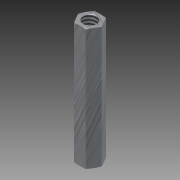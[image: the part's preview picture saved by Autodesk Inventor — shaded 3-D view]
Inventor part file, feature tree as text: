
AUTODESK INVENTOR PART (.ipt)
format: ipt  version: 2012 (Build 160160000, 160)  size: 119,808 bytes
history: native  units: in
note: dims shown in document units (in); Inventor stores cm internally (conversion verified against a paired STEP export)
features: thread x2, other x1, imported_body x1
ambient origin geometry x8: Origin, YZ Plane, XZ Plane, XY Plane, X Axis, Y Axis, Z Axis, Center Point
feature tree (4):
  parser-record x1  (decoder bookkeeping rows leaked as tree rows — omitted from the tree; the rows remain in map.json)
  imported_body  "Base1"
  thread  "Thread1"  [1 undecoded]
  thread  "Thread2"  [1 undecoded]
note: 2 required parameter values undecoded (feature->parameter linkage not recoverable at this tier; creation-order binding heuristic only, values carry confidence <= 0.55)
